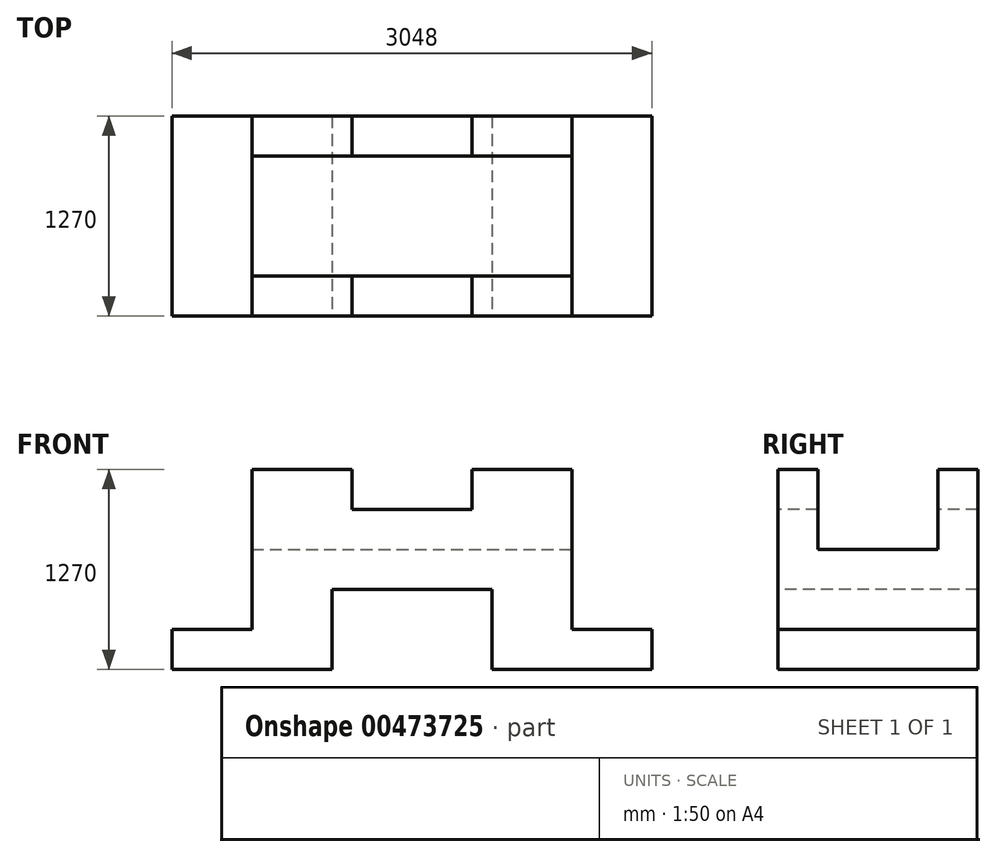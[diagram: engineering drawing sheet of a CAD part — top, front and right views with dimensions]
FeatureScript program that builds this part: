
annotation { "Feature Type Name" : "Feature", "Feature Type Description" : "" }
export const myFeature = defineFeature(function(context is Context, id is Id, definition is map)
    precondition{}
    {
        {
            var Q0;
            Q0=qCreatedBy(makeId("Front.planeOp"),FACE);
            var sketch = newSketch(context, id + "F0", { "sketchPlane" : qUnion([Q0])});
            skLineSegment(sketch, "E0.top", {"start": v(-1524, 1270) * mm, "end": v(1524, 1270) * mm});
            skLineSegment(sketch, "E0.left", {"start": v(-1524, 0) * mm, "end": v(-1524, 1270) * mm});
            skLineSegment(sketch, "E0.right", {"start": v(1524, 0) * mm, "end": v(1524, 1270) * mm});
            skPoint(sketch, "E0.middle", {"position": v(0, 0) * mm});
            skLineSegment(sketch, "E1", {"start": v(-1524, 0) * mm, "end": v(1524, 0) * mm});
            skPoint(sketch, "E2.orphan", {"position": v(1524, -1270) * mm});
            skPoint(sketch, "E3.orphan", {"position": v(-1524, -1270) * mm});
            skSolve(sketch);
        }
        {
            var Q0;
            Q0 = qSketchRegion(id + "F0", true);
            extrude(context, id + "F1", {"entities" : qUnion([Q0]), "endBound" : BoundingType.SYMMETRIC, "depth" : 1270 * mm});
        }
        {
            var Q0;
            Q0=makeQuery(id+"F1.opExtrude","CAP_FACE",FACE,{"disambiguationData":[OSD([sQuery(id+"F0.wireOp",EDGE,"E0.top"),sQuery(id+"F0.wireOp",EDGE,"E0.left"),sQuery(id+"F0.wireOp",EDGE,"E0.right"),sQuery(id+"F0.wireOp",EDGE,"E1")])],"isStart":false});
            var sketch = newSketch(context, id + "F2", { "sketchPlane" : qUnion([Q0])});
            skLineSegment(sketch, "E4.bottom", {"start": v(1524, 1270) * mm, "end": v(1016, 1270) * mm});
            skLineSegment(sketch, "E4.top", {"start": v(1524, 254) * mm, "end": v(1016, 254) * mm});
            skLineSegment(sketch, "E4.left", {"start": v(1524, 1270) * mm, "end": v(1524, 254) * mm});
            skLineSegment(sketch, "E4.right", {"start": v(1016, 1270) * mm, "end": v(1016, 254) * mm});
            skLineSegment(sketch, "E5.bottom", {"start": v(0, 0) * mm, "end": v(508, 0) * mm});
            skLineSegment(sketch, "E5.top", {"start": v(0, 508) * mm, "end": v(508, 508) * mm});
            skLineSegment(sketch, "E5.right", {"start": v(508, 0) * mm, "end": v(508, 508) * mm});
            skLineSegment(sketch, "E6.bottom", {"start": v(0, 1270) * mm, "end": v(381, 1270) * mm});
            skLineSegment(sketch, "E6.top", {"start": v(0, 1016) * mm, "end": v(381, 1016) * mm});
            skLineSegment(sketch, "E6.right", {"start": v(381, 1270) * mm, "end": v(381, 1016) * mm});
            skLineSegment(sketch, "E7.MirrorCS", {"start": v(0, 508) * mm, "end": v(-508, 508) * mm});
            skLineSegment(sketch, "E8.MirrorCS", {"start": v(0, 0) * mm, "end": v(-508, 0) * mm});
            skLineSegment(sketch, "E9.MirrorCS", {"start": v(-1016, 1270) * mm, "end": v(-1016, 254) * mm});
            skLineSegment(sketch, "E10.MirrorCS", {"start": v(-1524, 1270) * mm, "end": v(-1524, 254) * mm});
            skLineSegment(sketch, "E11.MirrorCS", {"start": v(-1524, 254) * mm, "end": v(-1016, 254) * mm});
            skLineSegment(sketch, "E12.MirrorCS", {"start": v(-1524, 1270) * mm, "end": v(-1016, 1270) * mm});
            skLineSegment(sketch, "E13.MirrorCS", {"start": v(0, 1270) * mm, "end": v(-381, 1270) * mm});
            skLineSegment(sketch, "E14.MirrorCS", {"start": v(0, 1016) * mm, "end": v(-381, 1016) * mm});
            skLineSegment(sketch, "E15.MirrorCS", {"start": v(-381, 1270) * mm, "end": v(-381, 1016) * mm});
            skLineSegment(sketch, "E16.MirrorCS", {"start": v(-508, 0) * mm, "end": v(-508, 508) * mm});
            skSolve(sketch);
        }
        {
            var Q0;
            Q0 = qSketchRegion(id + "F2", true);
            extrude(context, id + "F3", {"entities" : qUnion([Q0]), "operationType" : NewBodyOperationType.REMOVE, "endBound" : BoundingType.THROUGH_ALL, "oppositeDirection" : true, "depth" : 25.4 * mm});
        }
        {
            var Q0;
            Q0=makeQuery(id+"F3.boolean.opBoolean","COPY",FACE,{"derivedFrom":makeQuery(id+"F3.opExtrude","SWEPT_FACE",FACE,{"disambiguationData":[OSD([sQuery(id+"F2.wireOp",EDGE,"E4.right")])]})});
            var sketch = newSketch(context, id + "F4", { "sketchPlane" : qUnion([Q0])});
            skLineSegment(sketch, "E17.bottom", {"start": v(0, 1270) * mm, "end": v(381, 1270) * mm});
            skLineSegment(sketch, "E17.top", {"start": v(0, 762) * mm, "end": v(381, 762) * mm});
            skLineSegment(sketch, "E17.right", {"start": v(381, 1270) * mm, "end": v(381, 762) * mm});
            skLineSegment(sketch, "E18.MirrorCS", {"start": v(-381, 1270) * mm, "end": v(-381, 762) * mm});
            skLineSegment(sketch, "E19.MirrorCS", {"start": v(0, 1270) * mm, "end": v(-381, 1270) * mm});
            skLineSegment(sketch, "E20.MirrorCS", {"start": v(0, 762) * mm, "end": v(-381, 762) * mm});
            skSolve(sketch);
        }
        {
            var Q0;
            Q0 = qSketchRegion(id + "F4", true);
            extrude(context, id + "F5", {"entities" : qUnion([Q0]), "operationType" : NewBodyOperationType.REMOVE, "endBound" : BoundingType.THROUGH_ALL, "oppositeDirection" : true, "depth" : 25.4 * mm});
        }
    });
